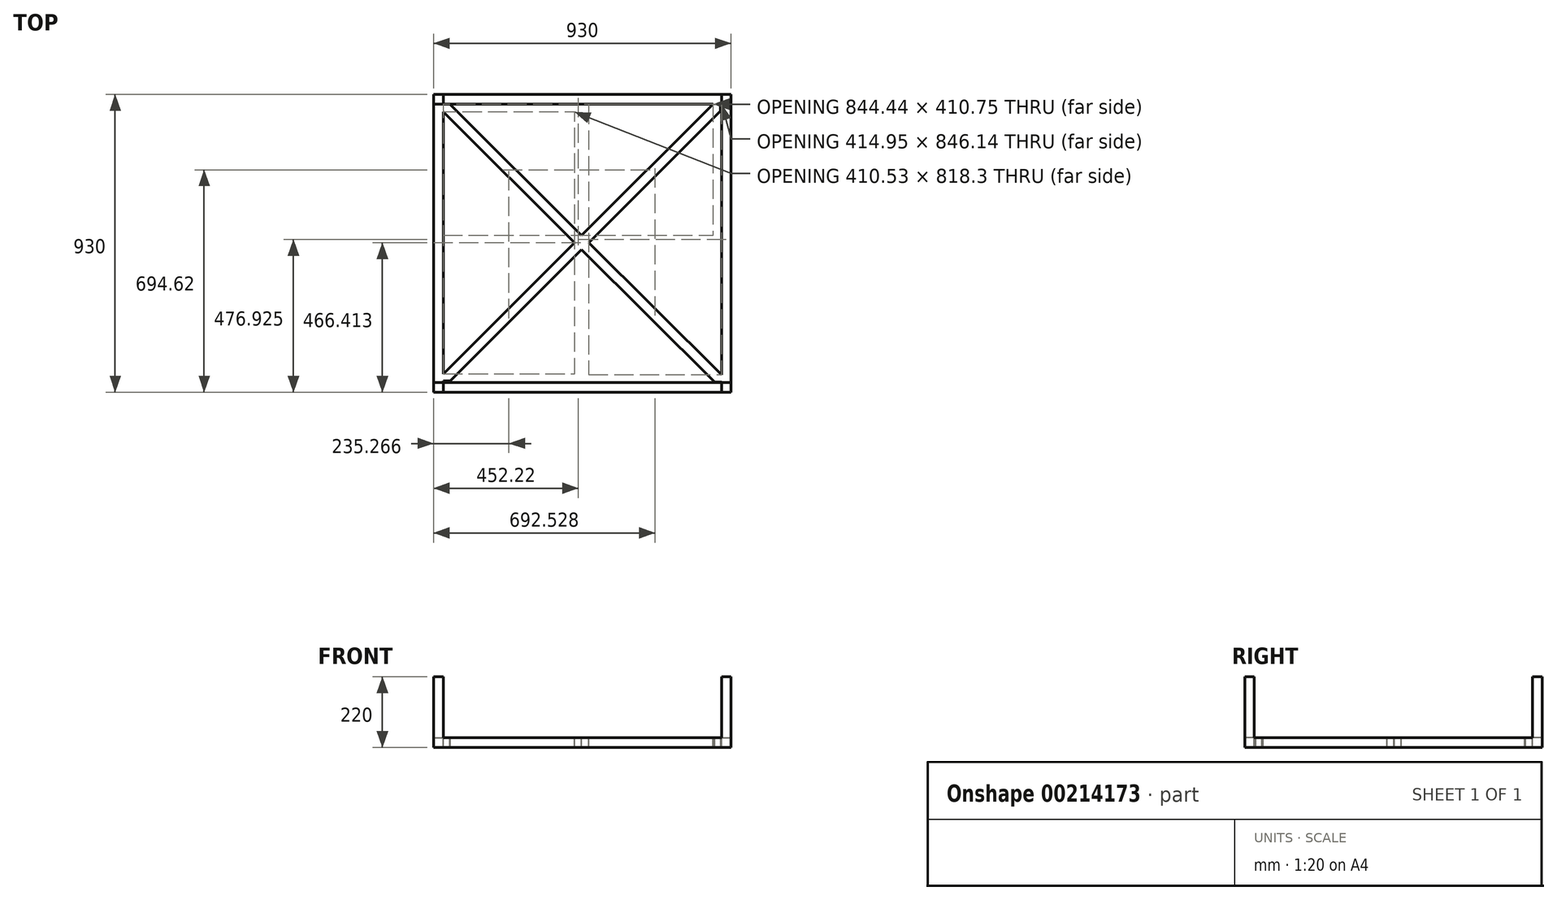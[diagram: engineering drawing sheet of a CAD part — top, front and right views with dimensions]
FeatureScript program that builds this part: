
annotation { "Feature Type Name" : "Feature", "Feature Type Description" : "" }
export const myFeature = defineFeature(function(context is Context, id is Id, definition is map)
    precondition{}
    {
        {
            var Q0;
            Q0=qCreatedBy(makeId("Top.planeOp"),FACE);
            var sketch = newSketch(context, id + "F0", { "sketchPlane" : qUnion([Q0])});
            skLineSegment(sketch, "E0.bottom", {"start": v(-450.56, 829.42) * mm, "end": v(449.44, 829.42) * mm});
            skLineSegment(sketch, "E0.top", {"start": v(-450.56, 799.42) * mm, "end": v(449.44, 799.42) * mm});
            skLineSegment(sketch, "E0.left", {"start": v(-450.56, 829.42) * mm, "end": v(-450.56, 799.42) * mm});
            skLineSegment(sketch, "E0.right", {"start": v(449.44, 829.42) * mm, "end": v(449.44, 799.42) * mm});
            skLineSegment(sketch, "E1.bottom", {"start": v(-450.56, 799.42) * mm, "end": v(-420.56, 799.42) * mm});
            skLineSegment(sketch, "E1.top", {"start": v(-450.56, -100.58) * mm, "end": v(-420.56, -100.58) * mm});
            skLineSegment(sketch, "E1.left", {"start": v(-450.56, 799.42) * mm, "end": v(-450.56, -100.58) * mm});
            skLineSegment(sketch, "E1.right", {"start": v(-420.56, 799.42) * mm, "end": v(-420.56, -100.58) * mm});
            skLineSegment(sketch, "E2.bottom", {"start": v(-420.56, -100.58) * mm, "end": v(479.44, -100.58) * mm});
            skLineSegment(sketch, "E2.top", {"start": v(-420.56, -70.58) * mm, "end": v(479.44, -70.58) * mm});
            skLineSegment(sketch, "E2.left", {"start": v(-420.56, -100.58) * mm, "end": v(-420.56, -70.58) * mm});
            skLineSegment(sketch, "E2.right", {"start": v(479.44, -100.58) * mm, "end": v(479.44, -70.58) * mm});
            skLineSegment(sketch, "E3.bottom", {"start": v(449.44, 829.42) * mm, "end": v(479.44, 829.42) * mm});
            skLineSegment(sketch, "E3.top", {"start": v(449.44, -70.58) * mm, "end": v(479.44, -70.58) * mm});
            skLineSegment(sketch, "E3.left", {"start": v(449.44, 829.42) * mm, "end": v(449.44, -70.58) * mm});
            skLineSegment(sketch, "E3.right", {"start": v(479.44, 829.42) * mm, "end": v(479.44, -70.58) * mm});
            skLineSegment(sketch, "E4", {"start": v(449.44, 799.42) * mm, "end": v(479.44, 799.42) * mm});
            skLineSegment(sketch, "E5", {"start": v(479.44, 799.42) * mm, "end": v(479.44, 829.42) * mm});
            skLineSegment(sketch, "E6", {"start": v(-420.56, 799.42) * mm, "end": v(-420.56, 829.42) * mm});
            skLineSegment(sketch, "E7", {"start": v(479.44, 829.42) * mm, "end": v(449.44, 829.42) * mm});
            skLineSegment(sketch, "E8", {"start": v(-450.56, -70.58) * mm, "end": v(-450.56, -100.58) * mm});
            skLineSegment(sketch, "E9", {"start": v(-450.56, -70.58) * mm, "end": v(-420.56, -70.58) * mm});
            skLineSegment(sketch, "E10", {"start": v(479.44, -70.58) * mm, "end": v(449.44, -70.58) * mm});
            skLineSegment(sketch, "E11", {"start": v(449.44, -70.58) * mm, "end": v(449.44, -100.58) * mm});
            skSolve(sketch);
        }
        {
            var Q0;
            {var subQ0=sQuery(id+"F0.wireOp",EDGE,"E0.top");Q0=makeQuery(id+"F0.imprint","IMPRINT",FACE,{"disambiguationData":[TD([[makeQuery(id+"F0.imprint","IMPRINT",EDGE,{"derivedFrom":subQ0}),-1.0]])]});}
            var sketch = newSketch(context, id + "F1", { "sketchPlane" : qUnion([Q0])});
            skLineSegment(sketch, "E12", {"start": v(-420.98, -65.9) * mm, "end": v(-420.98, -43.74) * mm});
            skLineSegment(sketch, "E13", {"start": v(-420.98, -65.9) * mm, "end": v(-398.82, -65.9) * mm});
            skLineSegment(sketch, "E14", {"start": v(446.45, 799.84) * mm, "end": v(446.45, 777.68) * mm});
            skLineSegment(sketch, "E15", {"start": v(446.45, 799.84) * mm, "end": v(424.3, 799.84) * mm});
            skLineSegment(sketch, "E16", {"start": v(424.3, 799.84) * mm, "end": v(446.45, 777.68) * mm});
            skLineSegment(sketch, "E17", {"start": v(449.86, -69.3) * mm, "end": v(449.86, -47.15) * mm});
            skLineSegment(sketch, "E18", {"start": v(449.86, -69.3) * mm, "end": v(427.7, -69.3) * mm});
            skLineSegment(sketch, "E19", {"start": v(427.7, -69.3) * mm, "end": v(449.86, -47.15) * mm});
            skLineSegment(sketch, "E20", {"start": v(-422.4, 799.26) * mm, "end": v(-422.4, 776.82) * mm});
            skLineSegment(sketch, "E21", {"start": v(-422.4, 799.26) * mm, "end": v(-399.96, 799.26) * mm});
            skLineSegment(sketch, "E22", {"start": v(-422.4, 776.82) * mm, "end": v(-399.96, 799.26) * mm});
            skLineSegment(sketch, "E23", {"start": v(-422.4, 776.82) * mm, "end": v(427.7, -69.3) * mm});
            skLineSegment(sketch, "E24", {"start": v(-399.96, 799.26) * mm, "end": v(449.86, -47.15) * mm});
            skLineSegment(sketch, "E25", {"start": v(-398.82, -65.9) * mm, "end": v(446.45, 777.68) * mm});
            skLineSegment(sketch, "E26", {"start": v(-420.98, -43.74) * mm, "end": v(424.3, 799.84) * mm});
            skSolve(sketch);
        }
        {
            var Q0;
            Q0 = qSketchRegion(id + "F0", true);
            extrude(context, id + "F2", {"entities" : qUnion([Q0]), "oppositeDirection" : true, "depth" : 30 * mm});
        }
        {
            var Q0;
            Q0 = qSketchRegion(id + "F1", true);
            extrude(context, id + "F3", {"entities" : qUnion([Q0]), "operationType" : NewBodyOperationType.ADD, "oppositeDirection" : true, "depth" : 30 * mm});
        }
        {
            var Q0;
            Q0=makeQuery(id+"F3.boolean.opBoolean","MERGE",FACE,{"derivedFrom":[makeQuery(id+"F2.opExtrude","CAP_FACE",FACE,{"disambiguationData":[OSD([sQuery(id+"F0.wireOp",EDGE,"E0.bottom"),sQuery(id+"F0.wireOp",EDGE,"E0.top"),sQuery(id+"F0.wireOp",EDGE,"E1.top"),sQuery(id+"F0.wireOp",EDGE,"E1.left"),sQuery(id+"F0.wireOp",EDGE,"E1.right"),sQuery(id+"F0.wireOp",EDGE,"E2.bottom"),sQuery(id+"F0.wireOp",EDGE,"E2.top"),sQuery(id+"F0.wireOp",EDGE,"E2.right"),sQuery(id+"F0.wireOp",EDGE,"E3.left"),sQuery(id+"F0.wireOp",EDGE,"E3.right"),sQuery(id+"F0.wireOp",EDGE,"E5"),sQuery(id+"F0.wireOp",EDGE,"E0.left"),sQuery(id+"F0.wireOp",EDGE,"E7"),sQuery(id+"F0.wireOp",EDGE,"E8")])],"isStart":true}),makeQuery(id+"F3.opExtrude","CAP_FACE",FACE,{"disambiguationData":[OSD([sQuery(id+"F1.wireOp",EDGE,"GX3NhK3j-k9a9-qD3W-rPyh-CovMWG9UslFr"),sQuery(id+"F1.wireOp",EDGE,"nL2ckCAE-UEZc-YeKt-ThJt-JJpOXjltlk4U"),sQuery(id+"F1.wireOp",EDGE,"gZ0eXNbP-d8Kc-IfvG-p2fw-uukFqkkNpnj0"),sQuery(id+"F1.wireOp",EDGE,"Grs3SFnu-PRV6-7StV-vJ0T-SITne5gj3QRc"),sQuery(id+"F1.wireOp",EDGE,"cxO1Tcob-ncb0-hcfJ-Rfzo-VWEH2sxEpGXs"),sQuery(id+"F1.wireOp",EDGE,"6F7Qi7ck-6i8t-8zJr-CoTz-qGXXOUwYOlc6"),sQuery(id+"F1.wireOp",EDGE,"9p3lRHFe-gMvR-YBKx-0UFj-galVOHitSzqP"),sQuery(id+"F1.wireOp",EDGE,"h4Kt6lBC-uURY-j1VZ-D2KP-zwB6W491qcmW")])],"isStart":true})]});
            var sketch = newSketch(context, id + "F4", { "sketchPlane" : qUnion([Q0])});
            skLineSegment(sketch, "E27.bottom", {"start": v(-450.56, 829.42) * mm, "end": v(-420.56, 829.42) * mm});
            skLineSegment(sketch, "E27.top", {"start": v(-450.56, 799.42) * mm, "end": v(-420.56, 799.42) * mm});
            skLineSegment(sketch, "E27.left", {"start": v(-450.56, 829.42) * mm, "end": v(-450.56, 799.42) * mm});
            skLineSegment(sketch, "E27.right", {"start": v(-420.56, 829.42) * mm, "end": v(-420.56, 799.42) * mm});
            skLineSegment(sketch, "E28.bottom", {"start": v(449.44, 799.42) * mm, "end": v(479.44, 799.42) * mm});
            skLineSegment(sketch, "E28.top", {"start": v(449.44, 829.42) * mm, "end": v(479.44, 829.42) * mm});
            skLineSegment(sketch, "E28.left", {"start": v(449.44, 799.42) * mm, "end": v(449.44, 829.42) * mm});
            skLineSegment(sketch, "E28.right", {"start": v(479.44, 799.42) * mm, "end": v(479.44, 829.42) * mm});
            skLineSegment(sketch, "E29.bottom", {"start": v(-450.56, -100.58) * mm, "end": v(-420.56, -100.58) * mm});
            skLineSegment(sketch, "E29.top", {"start": v(-450.56, -70.58) * mm, "end": v(-420.56, -70.58) * mm});
            skLineSegment(sketch, "E29.left", {"start": v(-450.56, -100.58) * mm, "end": v(-450.56, -70.58) * mm});
            skLineSegment(sketch, "E29.right", {"start": v(-420.56, -100.58) * mm, "end": v(-420.56, -70.58) * mm});
            skLineSegment(sketch, "E30.bottom", {"start": v(449.44, -70.58) * mm, "end": v(479.44, -70.58) * mm});
            skLineSegment(sketch, "E30.top", {"start": v(449.44, -100.58) * mm, "end": v(479.44, -100.58) * mm});
            skLineSegment(sketch, "E30.left", {"start": v(449.44, -70.58) * mm, "end": v(449.44, -100.58) * mm});
            skLineSegment(sketch, "E30.right", {"start": v(479.44, -70.58) * mm, "end": v(479.44, -100.58) * mm});
            skSolve(sketch);
        }
        {
            var Q0;
            Q0=makeQuery(id+"F4.imprint","IMPRINT",FACE,{"disambiguationData":[TD([[makeQuery(id+"F4.imprint","IMPRINT",EDGE,{"derivedFrom":sQuery(id+"F4.wireOp",EDGE,"E28.bottom")}),1.0]])]});
            var Q1;
            Q1=makeQuery(id+"F4.imprint","IMPRINT",FACE,{"disambiguationData":[TD([[makeQuery(id+"F4.imprint","IMPRINT",EDGE,{"derivedFrom":sQuery(id+"F4.wireOp",EDGE,"E29.bottom")}),1.0]])]});
            var Q2;
            Q2=makeQuery(id+"F4.imprint","IMPRINT",FACE,{"disambiguationData":[TD([[makeQuery(id+"F4.imprint","IMPRINT",EDGE,{"derivedFrom":sQuery(id+"F4.wireOp",EDGE,"E30.bottom")}),-1.0]])]});
            var Q3;
            Q3=makeQuery(id+"F4.imprint","IMPRINT",FACE,{"disambiguationData":[TD([[makeQuery(id+"F4.imprint","IMPRINT",EDGE,{"derivedFrom":sQuery(id+"F4.wireOp",EDGE,"E27.bottom")}),-1.0]])]});
            extrude(context, id + "F5", {"entities" : qUnion([Q0, Q1, Q2, Q3]), "operationType" : NewBodyOperationType.ADD, "depth" : 190 * mm});
        }
        {
            var Q0;
            Q0 = qSketchRegion(id + "F1", true);
            extrude(context, id + "F6", {"entities" : qUnion([Q0]), "operationType" : NewBodyOperationType.ADD, "oppositeDirection" : true, "depth" : 15 * mm});
        }
    });
